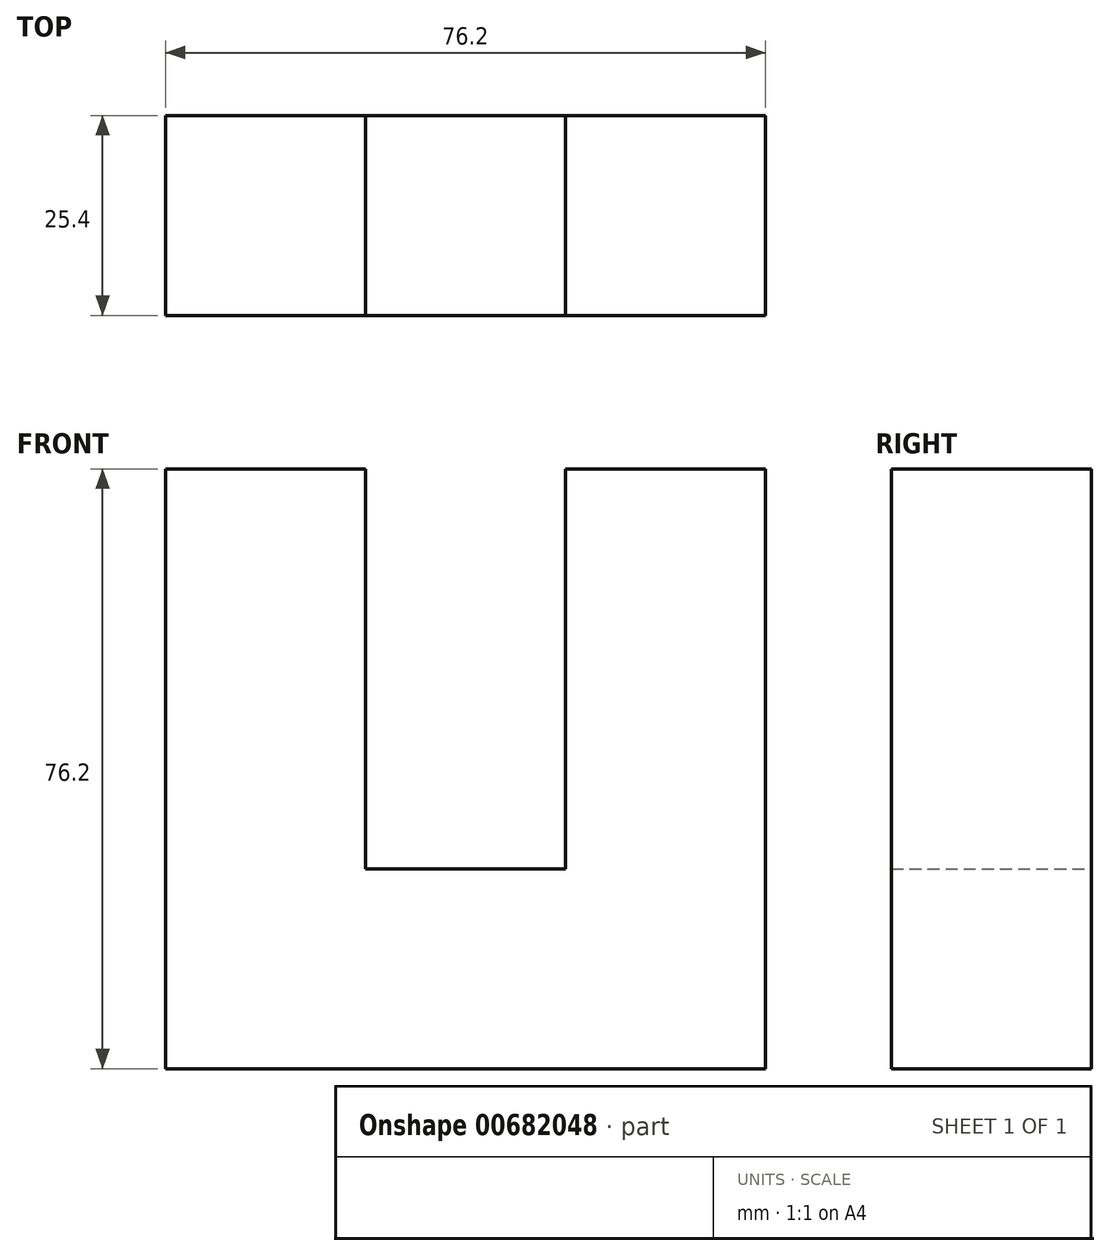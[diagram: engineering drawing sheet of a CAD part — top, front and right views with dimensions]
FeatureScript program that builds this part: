
annotation { "Feature Type Name" : "Feature", "Feature Type Description" : "" }
export const myFeature = defineFeature(function(context is Context, id is Id, definition is map)
    precondition{}
    {
        {
            var Q0;
            Q0=qCreatedBy(makeId("Front.planeOp"),FACE);
            var sketch = newSketch(context, id + "F0", { "sketchPlane" : qUnion([Q0])});
            skLineSegment(sketch, "E0", {"start": v(0, 0) * mm, "end": v(0, 76.2) * mm});
            skLineSegment(sketch, "E1", {"start": v(0, 0) * mm, "end": v(76.2, 0) * mm});
            skLineSegment(sketch, "E2", {"start": v(76.2, 0) * mm, "end": v(76.2, 76.2) * mm});
            skLineSegment(sketch, "E3", {"start": v(0, 76.2) * mm, "end": v(25.4, 76.2) * mm});
            skLineSegment(sketch, "E4", {"start": v(76.2, 76.2) * mm, "end": v(50.8, 76.2) * mm});
            skLineSegment(sketch, "E5", {"start": v(25.4, 76.2) * mm, "end": v(25.4, 25.4) * mm});
            skLineSegment(sketch, "E6", {"start": v(50.8, 76.2) * mm, "end": v(50.8, 25.4) * mm});
            skLineSegment(sketch, "E7", {"start": v(25.4, 25.4) * mm, "end": v(50.8, 25.4) * mm});
            skSolve(sketch);
        }
        {
            var Q0;
            Q0 = qSketchRegion(id + "F0", true);
            extrude(context, id + "F1", {"entities" : qUnion([Q0]), "depth" : 25.4 * mm, "offsetDistance" : 25.4 * mm});
        }
    });
